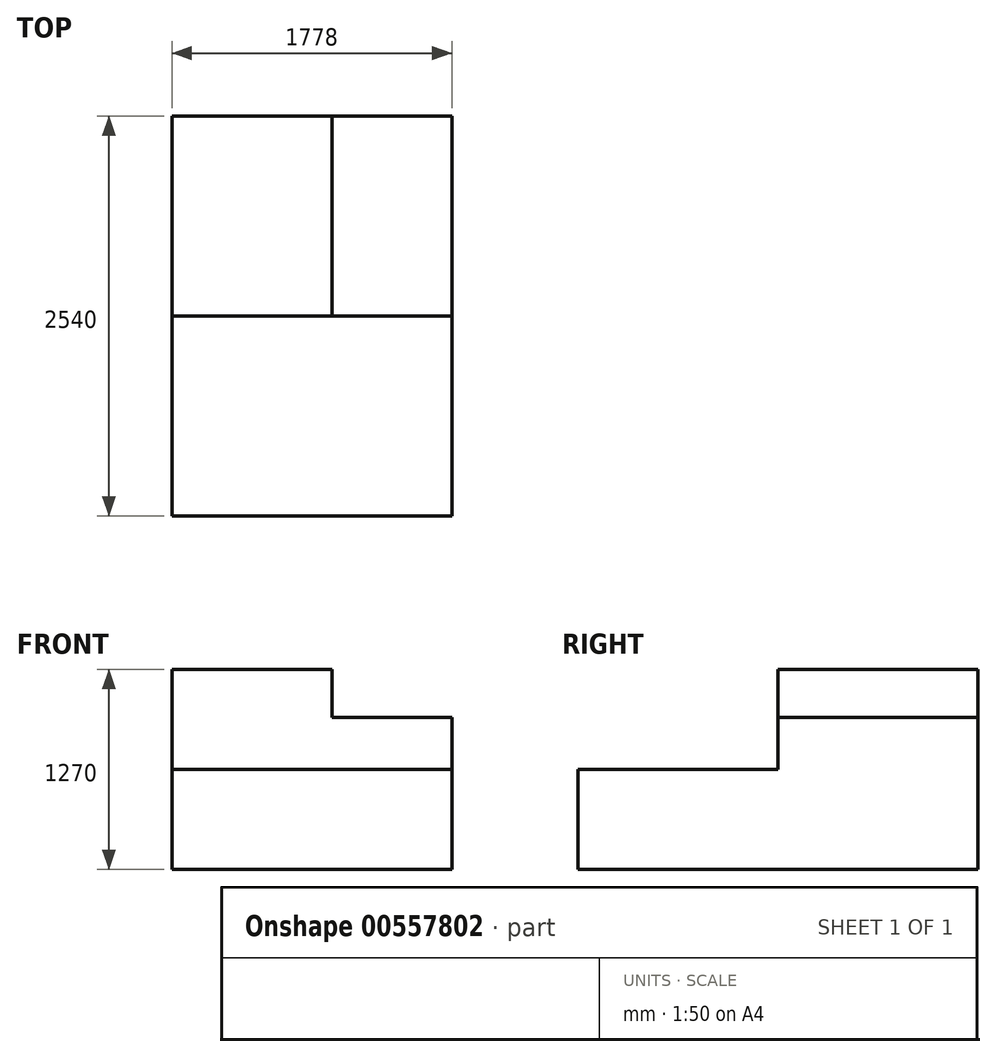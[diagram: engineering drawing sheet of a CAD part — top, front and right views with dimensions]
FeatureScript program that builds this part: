
annotation { "Feature Type Name" : "Feature", "Feature Type Description" : "" }
export const myFeature = defineFeature(function(context is Context, id is Id, definition is map)
    precondition{}
    {
        {
            var Q0;
            Q0=qCreatedBy(makeId("Right.planeOp"),FACE);
            var sketch = newSketch(context, id + "F0", { "sketchPlane" : qUnion([Q0])});
            skLineSegment(sketch, "E0", {"start": v(-54.36, -53.45) * mm, "end": v(-54.36, 581.55) * mm});
            skLineSegment(sketch, "E1", {"start": v(-54.36, 581.55) * mm, "end": v(1215.64, 581.55) * mm});
            skLineSegment(sketch, "E2", {"start": v(1215.64, 581.55) * mm, "end": v(1215.64, 911.75) * mm});
            skLineSegment(sketch, "E3", {"start": v(1215.64, 911.75) * mm, "end": v(2485.64, 911.75) * mm});
            skLineSegment(sketch, "E4", {"start": v(2485.64, 911.75) * mm, "end": v(2485.64, -53.45) * mm});
            skLineSegment(sketch, "E5", {"start": v(2485.64, -53.45) * mm, "end": v(-54.36, -53.45) * mm});
            skSolve(sketch);
        }
        {
            var Q0;
            Q0=makeQuery(id+"F0.imprint","IMPRINT",FACE,{"disambiguationData":[TD([[makeQuery(id+"F0.imprint","IMPRINT",EDGE,{"derivedFrom":sQuery(id+"F0.wireOp",EDGE,"E0")}),-1.0]])]});
            extrude(context, id + "F1", {"entities" : qUnion([Q0]), "oppositeDirection" : true, "depth" : 1778 * mm, "offsetDistance" : 25.4 * mm});
        }
        {
            var Q0;
            Q0=makeQuery(id+"F1.opExtrude","SWEPT_FACE",FACE,{"disambiguationData":[OSD([sQuery(id+"F0.wireOp",EDGE,"E3")])]});
            var sketch = newSketch(context, id + "F2", { "sketchPlane" : qUnion([Q0])});
            skLineSegment(sketch, "E6", {"start": v(-1778, 1215.64) * mm, "end": v(-762, 1215.64) * mm});
            skLineSegment(sketch, "E7", {"start": v(-762, 1215.64) * mm, "end": v(-762, 2485.64) * mm});
            skSolve(sketch);
        }
        {
            var Q0;
            Q0=makeQuery(id+"F2.imprint","IMPRINT",FACE,{"disambiguationData":[TD([[makeQuery(id+"F2.imprint","IMPRINT",EDGE,{"derivedFrom":sQuery(id+"F2.wireOp",EDGE,"E6")}),1.0]])]});
            extrude(context, id + "F3", {"entities" : qUnion([Q0]), "operationType" : NewBodyOperationType.ADD, "depth" : 304.8 * mm, "offsetDistance" : 25.4 * mm});
        }
    });
